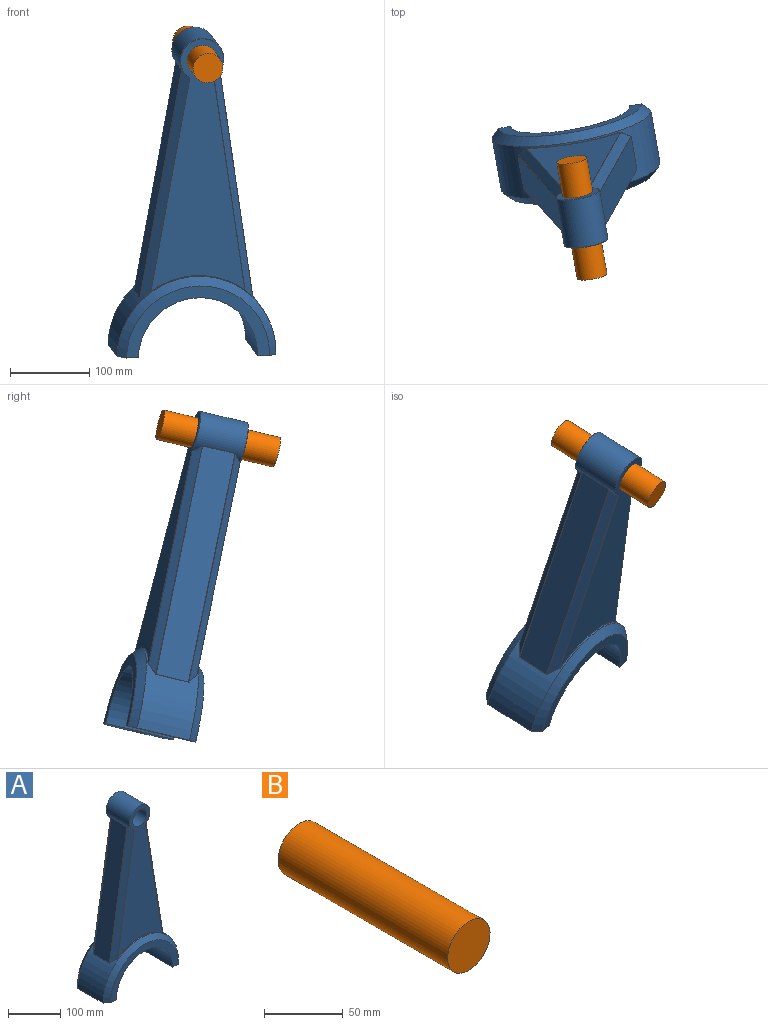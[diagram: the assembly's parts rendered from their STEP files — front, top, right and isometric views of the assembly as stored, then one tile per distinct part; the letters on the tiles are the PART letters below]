
ASSEMBLY  parts=2 mates=1
PART A: 62 faces, bbox 203.2x88.9x410.1 mm
  f0: cylinder r=101.6mm len=203.2mm, axis (0,1,0), area 11916.8mm2, adj f5,f7,f12,f13,f18,f19,f20,f21
  f1: plane 326.21x120mm, normal (0,-1,0), area 20273.9mm2, adj f8,f18,f22,f23,f24,f27,f28
  f2: plane 326.21x120mm, normal (0,1,0), area 20273.9mm2, adj f8,f46,f51,f54,f55,f56,f57
  f3: cylinder r=27.94mm len=62.56mm, axis (0,1,0), area 7529.3mm2, adj f23,f32,f33,f37,f38,f42,f43,f48
  f4: plane 294.87x47.59mm, normal (-0.99,0,0.16), area 12781.1mm2, adj f34,f35,f43,f44
  f5: plane 88.9x25.4mm, normal (0,0,-1), area 2028.2mm2, adj f0,f6,f10,f11,f12,f13,f60
  f6: cylinder r=76.2mm len=152.4mm, axis (0,1,0), area 21275.7mm2, adj f5,f7,f10,f11
  f7: plane 88.92x25.41mm, normal (-0.04,0,-1), area 2029.7mm2, adj f0,f6,f10,f11,f12,f13,f58
  f8: cylinder r=19.05mm len=63.5mm, axis (0,1,0), area 7600.6mm2, adj f1,f2
  f9: plane 296.04x48.41mm, normal (0.99,0,0.16), area 12836mm2, adj f30,f31,f41,f42
  f10: plane 182.88x92.1mm, normal (0,1,0), area 4017.4mm2, adj f5,f6,f7,f13
  f11: plane 182.88x92.1mm, normal (0,-1,0), area 4017.4mm2, adj f5,f6,f7,f12
  f12: cone r=101.6mm half-angle=45deg, axis (0,1,0), area 4369.2mm2, adj f0,f5,f7,f11
  f13: cone r=91.44mm half-angle=45deg, axis (0,-1,0), area 4369.2mm2, adj f0,f5,f7,f10
  f14: plane 295.34x56.82mm, normal (0.7,0.71,0.11), area 4032.5mm2, adj f40,f41,f51,f52
  f15: plane 295.34x56.82mm, normal (0.7,-0.71,0.11), area 4032.8mm2, adj f21,f22,f31,f32
  f16: plane 294.18x56.04mm, normal (-0.7,0.71,0.11), area 4018.3mm2, adj f44,f45,f53,f54
  f17: plane 294.18x56.05mm, normal (-0.7,-0.71,0.11), area 4018.1mm2, adj f24,f25,f33,f34
  f18: cone r=101.6mm half-angle=45deg, axis (0,1,0), area 85.1mm2, adj f0,f1,f19,f20
  f19: bspline ~0.95x0.77mm, area 0.5mm2, adj f0,f18,f21,f22
  f20: bspline ~0.94x0.76mm, area 0.5mm2, adj f0,f18,f24,f25
  f21: bspline ~11.69x10.51mm, area 8.3mm2, adj f0,f15,f19,f26
  f22: plane 275.89x45.45mm, normal (0.38,-0.92,0.06), area 100.5mm2, adj f1,f15,f19,f27
  f23: cone r=27.47mm half-angle=45deg, axis (0,1,0), area 92.8mm2, adj f1,f3,f27,f28
  f24: plane 275.15x44.75mm, normal (-0.38,-0.92,0.06), area 100.2mm2, adj f1,f17,f20,f28
  f25: bspline ~13.15x11.57mm, area 8.2mm2, adj f0,f17,f20,f29
  f26: bspline ~0.68x0.63mm, area 0.2mm2, adj f0,f21,f30,f31
  f27: bspline ~1.31x1mm, area 0.6mm2, adj f1,f22,f23,f32
  f28: bspline ~1.31x1mm, area 0.6mm2, adj f1,f23,f24,f33
  f29: bspline ~0.68x0.62mm, area 0.2mm2, adj f0,f25,f34,f35
  f30: plane 42.79x0.25mm, normal (0.89,0,0.45), area 12.1mm2, adj f0,f9,f26,f36
  f31: plane 296.05x48.5mm, normal (0.91,-0.38,0.15), area 107.4mm2, adj f9,f15,f26,f37
  f32: bspline ~11.54x10.81mm, area 7.8mm2, adj f3,f15,f27,f37
  f33: bspline ~10.22x9.39mm, area 7.8mm2, adj f3,f17,f28,f38
  f34: plane 294.88x47.69mm, normal (-0.91,-0.38,0.15), area 107.3mm2, adj f4,f17,f29,f38
  f35: plane 42.79x0.26mm, normal (-0.89,0,0.45), area 12.3mm2, adj f0,f4,f29,f39
  f36: bspline ~0.67x0.62mm, area 0.2mm2, adj f0,f30,f40,f41
  f37: bspline ~0.67x0.67mm, area 0.2mm2, adj f3,f31,f32,f42
  f38: bspline ~0.67x0.67mm, area 0.2mm2, adj f3,f33,f34,f43
  f39: bspline ~0.68x0.62mm, area 0.2mm2, adj f0,f35,f44,f45
  f40: bspline ~11.69x10.51mm, area 8.3mm2, adj f0,f14,f36,f47
  f41: plane 296.05x48.5mm, normal (0.91,0.38,0.15), area 107.4mm2, adj f9,f14,f36,f48
  f42: plane 42.79x0.31mm, normal (0.99,0,-0.17), area 13.2mm2, adj f3,f9,f37,f48
  f43: plane 42.79x0.31mm, normal (-0.98,0,-0.18), area 13.4mm2, adj f3,f4,f38,f49
  f44: plane 294.88x47.69mm, normal (-0.91,0.38,0.15), area 107.3mm2, adj f4,f16,f39,f49
  f45: bspline ~11.62x10.22mm, area 8.2mm2, adj f0,f16,f39,f50
  f46: cone r=102.07mm half-angle=45deg, axis (0,-1,0), area 85.1mm2, adj f0,f2,f47,f50
  f47: bspline ~0.95x0.77mm, area 0.5mm2, adj f0,f40,f46,f51
  f48: bspline ~0.67x0.67mm, area 0.2mm2, adj f3,f41,f42,f52
  f49: bspline ~0.67x0.66mm, area 0.2mm2, adj f3,f43,f44,f53
  f50: bspline ~0.94x0.76mm, area 0.5mm2, adj f0,f45,f46,f54
  f51: plane 275.89x45.45mm, normal (0.38,0.92,0.06), area 100.5mm2, adj f2,f14,f47,f55
  f52: bspline ~10.22x9.49mm, area 7.8mm2, adj f3,f14,f48,f55
  f53: bspline ~10.22x9.38mm, area 7.8mm2, adj f3,f16,f49,f56
  f54: plane 275.15x44.75mm, normal (-0.38,0.92,0.06), area 100.2mm2, adj f2,f16,f50,f56
  f55: bspline ~1.31x1mm, area 0.6mm2, adj f2,f51,f52,f57
  f56: bspline ~1.31x1mm, area 0.6mm2, adj f2,f53,f54,f57
  f57: cone r=27.94mm half-angle=45deg, axis (0,-1,0), area 92.7mm2, adj f2,f3,f55,f56
  f58: cylinder r=6.35mm len=23.39mm, axis (-0.04,0,-1), area 912.1mm2, adj f7,f59
  f59: plane 12.7x12.69mm, normal (-0.04,0,-1), area 126.7mm2, adj f58
  f60: cylinder r=6.35mm len=22.89mm, axis (0,0,-1), area 912.1mm2, adj f5,f61
  f61: plane 12.7x12.7mm, normal (0,0,-1), area 126.7mm2, adj f60
PART B: 3 faces, bbox 38.1x152.4x38.1 mm
  f0: cylinder r=19.05mm len=152.4mm, axis (0,1,0), area 18241.5mm2, adj f1,f2
  f1: plane 38.1x38.1mm, normal (0,-1,0), area 1140.1mm2, adj f0
  f2: plane 38.1x38.1mm, normal (0,1,0), area 1140.1mm2, adj f0
PLACE A rot(axis=(0.8,0,0.6),16.4deg) t=(175.16,125.28,78.7)mm
PLACE B rot(axis=(0.4,-0.91,0.13),40deg) t=(187.94,8.47,442.52)mm
MATE revolute B.f0 <-> A.f8  axis (-0.17,0.96,0.23) through (187.94,8.47,442.52)mm
